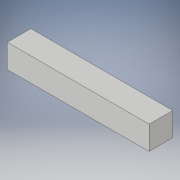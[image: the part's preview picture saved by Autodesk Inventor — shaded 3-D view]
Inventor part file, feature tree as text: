
AUTODESK INVENTOR PART (.ipt)
format: ipt  version: 2018 (Build 220112000, 112)  size: 90,624 bytes
history: native  units: in
note: dims shown in document units (in); Inventor stores cm internally (conversion verified against a paired STEP export)
features: extrude x1, sketch x1
ambient origin geometry x8: Origin, YZ Plane, XZ Plane, XY Plane, X Axis, Y Axis, Z Axis, Center Point
bodies: Solid1 (feature_tree)
feature tree (2):
  extrude  "Extrusion1"  Depth=2.0in
  sketch  "Sketch1"  dims[d0=2.0in d1=2.0in d2=12.0in d3=0.0in]
